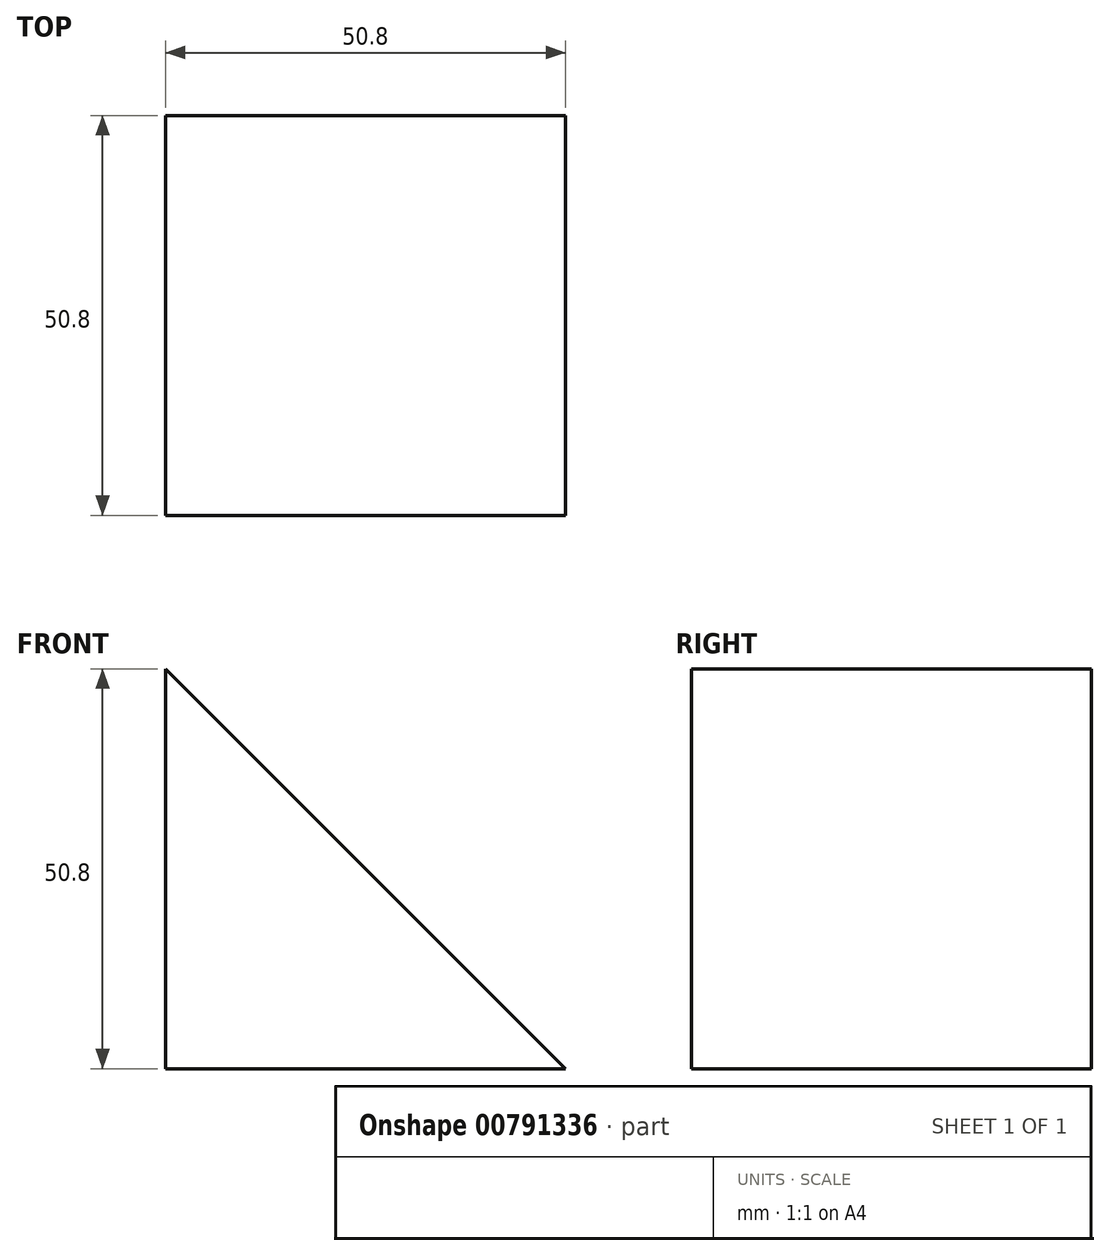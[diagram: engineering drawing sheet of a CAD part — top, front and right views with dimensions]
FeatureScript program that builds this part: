
annotation { "Feature Type Name" : "Feature", "Feature Type Description" : "" }
export const myFeature = defineFeature(function(context is Context, id is Id, definition is map)
    precondition{}
    {
        {
            var Q0;
            Q0=qCreatedBy(makeId("Front.planeOp"),FACE);
            var sketch = newSketch(context, id + "F0", { "sketchPlane" : qUnion([Q0])});
            skLineSegment(sketch, "E0", {"start": v(0, 0) * mm, "end": v(50.8, 0) * mm});
            skLineSegment(sketch, "E1", {"start": v(50.8, 0) * mm, "end": v(0, 0) * mm});
            skLineSegment(sketch, "E2", {"start": v(0, 0) * mm, "end": v(0, 50.8) * mm});
            skLineSegment(sketch, "E3", {"start": v(0, 50.8) * mm, "end": v(50.8, 0) * mm});
            skSolve(sketch);
        }
        {
            var Q0;
            Q0=qSketchRegion(id+"F0",true);
            extrude(context, id + "F1", {"entities" : qUnion([Q0]), "depth" : 50.8 * mm, "offsetDistance" : 25.4 * mm});
        }
    });
